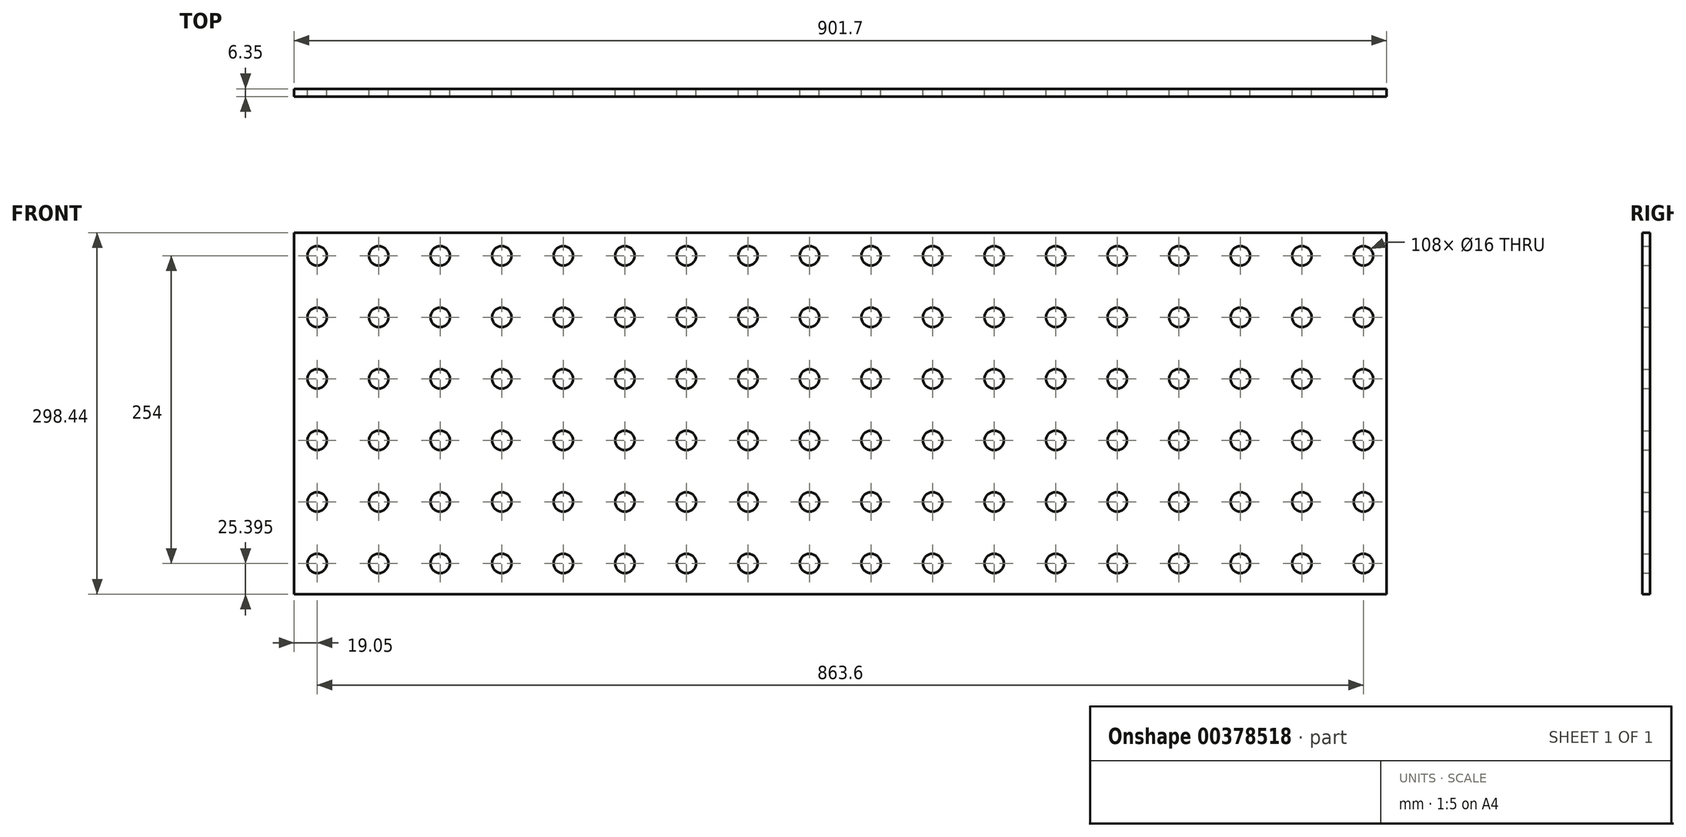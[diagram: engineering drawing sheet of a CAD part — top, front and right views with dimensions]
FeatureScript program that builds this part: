
annotation { "Feature Type Name" : "Feature", "Feature Type Description" : "" }
export const myFeature = defineFeature(function(context is Context, id is Id, definition is map)
    precondition{}
    {
        {
            var Q0;
            Q0=qCreatedBy(makeId("Front.planeOp"),FACE);
            var sketch = newSketch(context, id + "F0", { "sketchPlane" : qUnion([Q0])});
            skLineSegment(sketch, "E0.bottom", {"start": v(450.85, 149.23) * mm, "end": v(-450.85, 149.23) * mm});
            skLineSegment(sketch, "E0.top", {"start": v(450.85, -149.23) * mm, "end": v(-450.85, -149.23) * mm});
            skLineSegment(sketch, "E0.left", {"start": v(450.85, 149.23) * mm, "end": v(450.85, -149.23) * mm});
            skLineSegment(sketch, "E0.right", {"start": v(-450.85, 149.23) * mm, "end": v(-450.85, -149.23) * mm});
            skPoint(sketch, "E0.middle", {"position": v(0, 0) * mm});
            skCircle(sketch, "E1", {"center": v(-431.8, -123.83) * mm, "radius": 8 * mm});
            skCircle(sketch, "E2.0.1.0", {"center": v(-431.8, -73.03) * mm, "radius": 8 * mm});
            skCircle(sketch, "E2.0.2.0", {"center": v(-431.8, -22.22) * mm, "radius": 8 * mm});
            skCircle(sketch, "E2.0.3.0", {"center": v(-431.8, 28.58) * mm, "radius": 8 * mm});
            skCircle(sketch, "E2.0.4.0", {"center": v(-431.8, 79.38) * mm, "radius": 8 * mm});
            skCircle(sketch, "E2.0.5.0", {"center": v(-431.8, 130.18) * mm, "radius": 8 * mm});
            skCircle(sketch, "E2.1.0.0", {"center": v(-381, -123.83) * mm, "radius": 8 * mm});
            skCircle(sketch, "E2.1.1.0", {"center": v(-381, -73.03) * mm, "radius": 8 * mm});
            skCircle(sketch, "E2.1.2.0", {"center": v(-381, -22.22) * mm, "radius": 8 * mm});
            skCircle(sketch, "E2.1.3.0", {"center": v(-381, 28.58) * mm, "radius": 8 * mm});
            skCircle(sketch, "E2.1.4.0", {"center": v(-381, 79.38) * mm, "radius": 8 * mm});
            skCircle(sketch, "E2.1.5.0", {"center": v(-381, 130.18) * mm, "radius": 8 * mm});
            skCircle(sketch, "E2.2.0.0", {"center": v(-330.2, -123.83) * mm, "radius": 8 * mm});
            skCircle(sketch, "E2.2.1.0", {"center": v(-330.2, -73.03) * mm, "radius": 8 * mm});
            skCircle(sketch, "E2.2.2.0", {"center": v(-330.2, -22.22) * mm, "radius": 8 * mm});
            skCircle(sketch, "E2.2.3.0", {"center": v(-330.2, 28.58) * mm, "radius": 8 * mm});
            skCircle(sketch, "E2.2.4.0", {"center": v(-330.2, 79.38) * mm, "radius": 8 * mm});
            skCircle(sketch, "E2.2.5.0", {"center": v(-330.2, 130.18) * mm, "radius": 8 * mm});
            skCircle(sketch, "E2.3.0.0", {"center": v(-279.4, -123.83) * mm, "radius": 8 * mm});
            skCircle(sketch, "E2.3.1.0", {"center": v(-279.4, -73.03) * mm, "radius": 8 * mm});
            skCircle(sketch, "E2.3.2.0", {"center": v(-279.4, -22.22) * mm, "radius": 8 * mm});
            skCircle(sketch, "E2.3.3.0", {"center": v(-279.4, 28.58) * mm, "radius": 8 * mm});
            skCircle(sketch, "E2.3.4.0", {"center": v(-279.4, 79.38) * mm, "radius": 8 * mm});
            skCircle(sketch, "E2.3.5.0", {"center": v(-279.4, 130.18) * mm, "radius": 8 * mm});
            skCircle(sketch, "E2.4.0.0", {"center": v(-228.6, -123.83) * mm, "radius": 8 * mm});
            skCircle(sketch, "E2.4.1.0", {"center": v(-228.6, -73.03) * mm, "radius": 8 * mm});
            skCircle(sketch, "E2.4.2.0", {"center": v(-228.6, -22.22) * mm, "radius": 8 * mm});
            skCircle(sketch, "E2.4.3.0", {"center": v(-228.6, 28.58) * mm, "radius": 8 * mm});
            skCircle(sketch, "E2.4.4.0", {"center": v(-228.6, 79.38) * mm, "radius": 8 * mm});
            skCircle(sketch, "E2.4.5.0", {"center": v(-228.6, 130.18) * mm, "radius": 8 * mm});
            skCircle(sketch, "E2.5.0.0", {"center": v(-177.8, -123.83) * mm, "radius": 8 * mm});
            skCircle(sketch, "E2.5.1.0", {"center": v(-177.8, -73.03) * mm, "radius": 8 * mm});
            skCircle(sketch, "E2.5.2.0", {"center": v(-177.8, -22.22) * mm, "radius": 8 * mm});
            skCircle(sketch, "E2.5.3.0", {"center": v(-177.8, 28.58) * mm, "radius": 8 * mm});
            skCircle(sketch, "E2.5.4.0", {"center": v(-177.8, 79.38) * mm, "radius": 8 * mm});
            skCircle(sketch, "E2.5.5.0", {"center": v(-177.8, 130.18) * mm, "radius": 8 * mm});
            skCircle(sketch, "E2.6.0.0", {"center": v(-127, -123.83) * mm, "radius": 8 * mm});
            skCircle(sketch, "E2.6.1.0", {"center": v(-127, -73.03) * mm, "radius": 8 * mm});
            skCircle(sketch, "E2.6.2.0", {"center": v(-127, -22.22) * mm, "radius": 8 * mm});
            skCircle(sketch, "E2.6.3.0", {"center": v(-127, 28.58) * mm, "radius": 8 * mm});
            skCircle(sketch, "E2.6.4.0", {"center": v(-127, 79.38) * mm, "radius": 8 * mm});
            skCircle(sketch, "E2.6.5.0", {"center": v(-127, 130.18) * mm, "radius": 8 * mm});
            skCircle(sketch, "E2.7.0.0", {"center": v(-76.2, -123.83) * mm, "radius": 8 * mm});
            skCircle(sketch, "E2.7.1.0", {"center": v(-76.2, -73.03) * mm, "radius": 8 * mm});
            skCircle(sketch, "E2.7.2.0", {"center": v(-76.2, -22.22) * mm, "radius": 8 * mm});
            skCircle(sketch, "E2.7.3.0", {"center": v(-76.2, 28.58) * mm, "radius": 8 * mm});
            skCircle(sketch, "E2.7.4.0", {"center": v(-76.2, 79.38) * mm, "radius": 8 * mm});
            skCircle(sketch, "E2.7.5.0", {"center": v(-76.2, 130.18) * mm, "radius": 8 * mm});
            skCircle(sketch, "E2.8.0.0", {"center": v(-25.4, -123.83) * mm, "radius": 8 * mm});
            skCircle(sketch, "E2.8.1.0", {"center": v(-25.4, -73.03) * mm, "radius": 8 * mm});
            skCircle(sketch, "E2.8.2.0", {"center": v(-25.4, -22.22) * mm, "radius": 8 * mm});
            skCircle(sketch, "E2.8.3.0", {"center": v(-25.4, 28.58) * mm, "radius": 8 * mm});
            skCircle(sketch, "E2.8.4.0", {"center": v(-25.4, 79.38) * mm, "radius": 8 * mm});
            skCircle(sketch, "E2.8.5.0", {"center": v(-25.4, 130.18) * mm, "radius": 8 * mm});
            skCircle(sketch, "E2.9.0.0", {"center": v(25.4, -123.83) * mm, "radius": 8 * mm});
            skCircle(sketch, "E2.9.1.0", {"center": v(25.4, -73.03) * mm, "radius": 8 * mm});
            skCircle(sketch, "E2.9.2.0", {"center": v(25.4, -22.22) * mm, "radius": 8 * mm});
            skCircle(sketch, "E2.9.3.0", {"center": v(25.4, 28.58) * mm, "radius": 8 * mm});
            skCircle(sketch, "E2.9.4.0", {"center": v(25.4, 79.38) * mm, "radius": 8 * mm});
            skCircle(sketch, "E2.9.5.0", {"center": v(25.4, 130.18) * mm, "radius": 8 * mm});
            skCircle(sketch, "E2.10.0.0", {"center": v(76.2, -123.83) * mm, "radius": 8 * mm});
            skCircle(sketch, "E2.10.1.0", {"center": v(76.2, -73.03) * mm, "radius": 8 * mm});
            skCircle(sketch, "E2.10.2.0", {"center": v(76.2, -22.22) * mm, "radius": 8 * mm});
            skCircle(sketch, "E2.10.3.0", {"center": v(76.2, 28.58) * mm, "radius": 8 * mm});
            skCircle(sketch, "E2.10.4.0", {"center": v(76.2, 79.38) * mm, "radius": 8 * mm});
            skCircle(sketch, "E2.10.5.0", {"center": v(76.2, 130.18) * mm, "radius": 8 * mm});
            skCircle(sketch, "E2.11.0.0", {"center": v(127, -123.83) * mm, "radius": 8 * mm});
            skCircle(sketch, "E2.11.1.0", {"center": v(127, -73.03) * mm, "radius": 8 * mm});
            skCircle(sketch, "E2.11.2.0", {"center": v(127, -22.22) * mm, "radius": 8 * mm});
            skCircle(sketch, "E2.11.3.0", {"center": v(127, 28.58) * mm, "radius": 8 * mm});
            skCircle(sketch, "E2.11.4.0", {"center": v(127, 79.38) * mm, "radius": 8 * mm});
            skCircle(sketch, "E2.11.5.0", {"center": v(127, 130.18) * mm, "radius": 8 * mm});
            skCircle(sketch, "E2.12.0.0", {"center": v(177.8, -123.83) * mm, "radius": 8 * mm});
            skCircle(sketch, "E2.12.1.0", {"center": v(177.8, -73.03) * mm, "radius": 8 * mm});
            skCircle(sketch, "E2.12.2.0", {"center": v(177.8, -22.22) * mm, "radius": 8 * mm});
            skCircle(sketch, "E2.12.3.0", {"center": v(177.8, 28.58) * mm, "radius": 8 * mm});
            skCircle(sketch, "E2.12.4.0", {"center": v(177.8, 79.38) * mm, "radius": 8 * mm});
            skCircle(sketch, "E2.12.5.0", {"center": v(177.8, 130.18) * mm, "radius": 8 * mm});
            skCircle(sketch, "E2.13.0.0", {"center": v(228.6, -123.83) * mm, "radius": 8 * mm});
            skCircle(sketch, "E2.13.1.0", {"center": v(228.6, -73.03) * mm, "radius": 8 * mm});
            skCircle(sketch, "E2.13.2.0", {"center": v(228.6, -22.22) * mm, "radius": 8 * mm});
            skCircle(sketch, "E2.13.3.0", {"center": v(228.6, 28.58) * mm, "radius": 8 * mm});
            skCircle(sketch, "E2.13.4.0", {"center": v(228.6, 79.38) * mm, "radius": 8 * mm});
            skCircle(sketch, "E2.13.5.0", {"center": v(228.6, 130.18) * mm, "radius": 8 * mm});
            skCircle(sketch, "E2.14.0.0", {"center": v(279.4, -123.83) * mm, "radius": 8 * mm});
            skCircle(sketch, "E2.14.1.0", {"center": v(279.4, -73.03) * mm, "radius": 8 * mm});
            skCircle(sketch, "E2.14.2.0", {"center": v(279.4, -22.22) * mm, "radius": 8 * mm});
            skCircle(sketch, "E2.14.3.0", {"center": v(279.4, 28.58) * mm, "radius": 8 * mm});
            skCircle(sketch, "E2.14.4.0", {"center": v(279.4, 79.38) * mm, "radius": 8 * mm});
            skCircle(sketch, "E2.14.5.0", {"center": v(279.4, 130.18) * mm, "radius": 8 * mm});
            skCircle(sketch, "E2.15.0.0", {"center": v(330.2, -123.83) * mm, "radius": 8 * mm});
            skCircle(sketch, "E2.15.1.0", {"center": v(330.2, -73.03) * mm, "radius": 8 * mm});
            skCircle(sketch, "E2.15.2.0", {"center": v(330.2, -22.22) * mm, "radius": 8 * mm});
            skCircle(sketch, "E2.15.3.0", {"center": v(330.2, 28.58) * mm, "radius": 8 * mm});
            skCircle(sketch, "E2.15.4.0", {"center": v(330.2, 79.38) * mm, "radius": 8 * mm});
            skCircle(sketch, "E2.15.5.0", {"center": v(330.2, 130.18) * mm, "radius": 8 * mm});
            skCircle(sketch, "E2.16.0.0", {"center": v(381, -123.83) * mm, "radius": 8 * mm});
            skCircle(sketch, "E2.16.1.0", {"center": v(381, -73.03) * mm, "radius": 8 * mm});
            skCircle(sketch, "E2.16.2.0", {"center": v(381, -22.22) * mm, "radius": 8 * mm});
            skCircle(sketch, "E2.16.3.0", {"center": v(381, 28.58) * mm, "radius": 8 * mm});
            skCircle(sketch, "E2.16.4.0", {"center": v(381, 79.38) * mm, "radius": 8 * mm});
            skCircle(sketch, "E2.16.5.0", {"center": v(381, 130.18) * mm, "radius": 8 * mm});
            skCircle(sketch, "E2.17.0.0", {"center": v(431.8, -123.83) * mm, "radius": 8 * mm});
            skCircle(sketch, "E2.17.1.0", {"center": v(431.8, -73.03) * mm, "radius": 8 * mm});
            skCircle(sketch, "E2.17.2.0", {"center": v(431.8, -22.22) * mm, "radius": 8 * mm});
            skCircle(sketch, "E2.17.3.0", {"center": v(431.8, 28.58) * mm, "radius": 8 * mm});
            skCircle(sketch, "E2.17.4.0", {"center": v(431.8, 79.38) * mm, "radius": 8 * mm});
            skCircle(sketch, "E2.17.5.0", {"center": v(431.8, 130.18) * mm, "radius": 8 * mm});
            skLineSegment(sketch, "E2.direction1", {"start": v(-431.8, -123.83) * mm, "end": v(-381, -123.83) * mm, "construction": true});
            skLineSegment(sketch, "E2.direction2", {"start": v(-431.8, -123.83) * mm, "end": v(-431.8, -73.03) * mm, "construction": true});
            skSolve(sketch);
        }
        {
            var Q0;
            Q0 = qSketchRegion(id + "F0", true);
            extrude(context, id + "F1", {"entities" : qUnion([Q0]), "depth" : 6.35 * mm});
        }
    });
